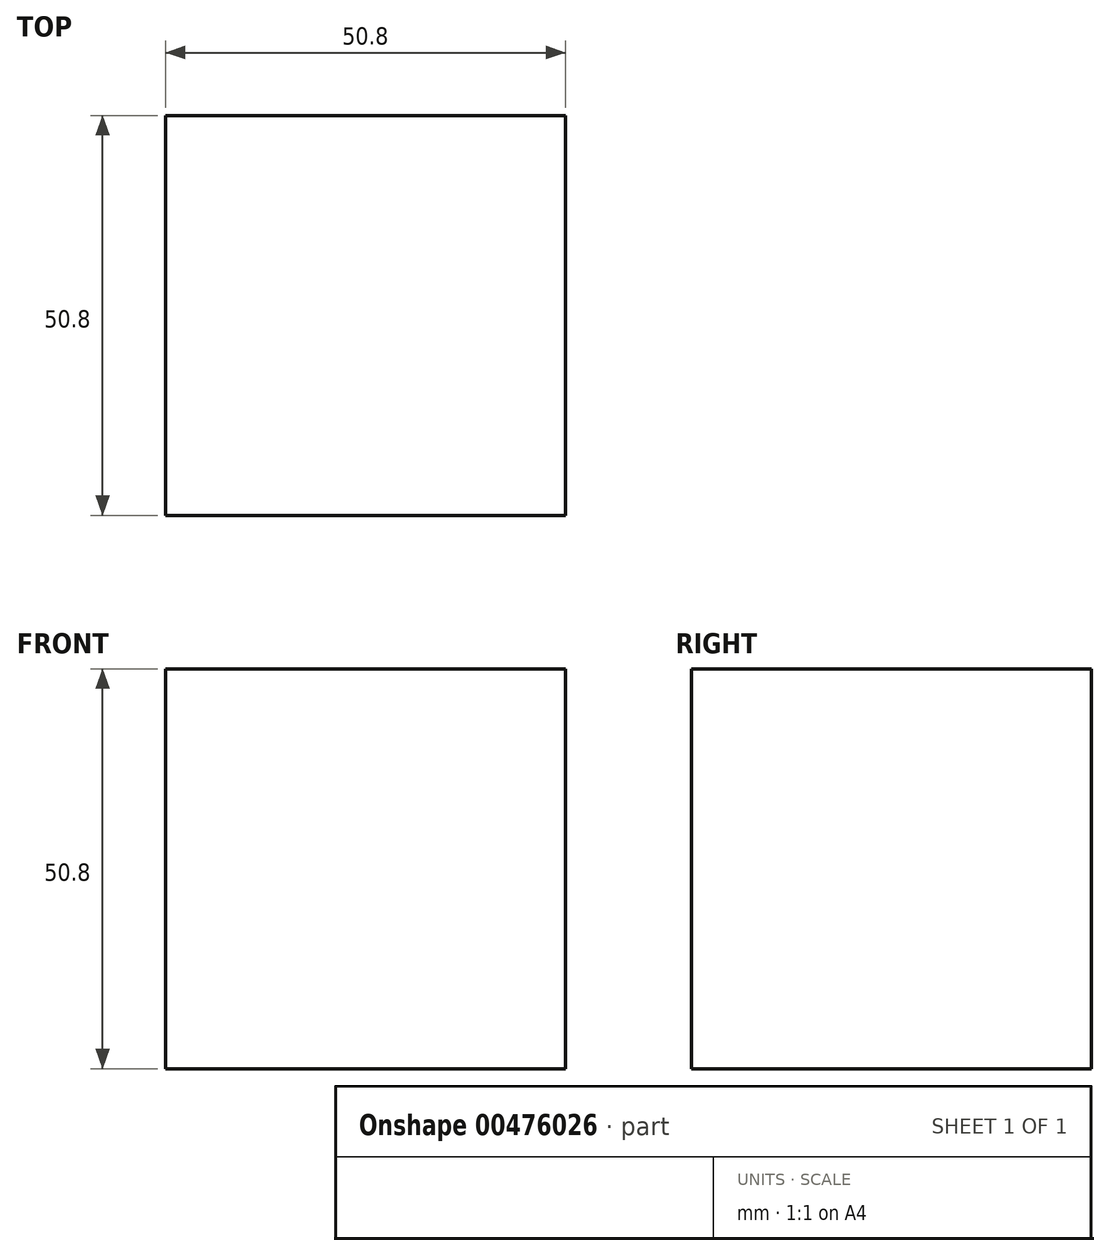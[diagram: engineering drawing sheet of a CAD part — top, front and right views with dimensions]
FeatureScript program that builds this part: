
annotation { "Feature Type Name" : "Feature", "Feature Type Description" : "" }
export const myFeature = defineFeature(function(context is Context, id is Id, definition is map)
    precondition{}
    {
        {
            var Q0;
            Q0=qCreatedBy(makeId("Front.planeOp"),FACE);
            var sketch = newSketch(context, id + "F0", { "sketchPlane" : qUnion([Q0])});
            skLineSegment(sketch, "E0.bottom", {"start": v(-32.94, 38.94) * mm, "end": v(17.86, 38.94) * mm});
            skLineSegment(sketch, "E0.top", {"start": v(-32.94, -11.86) * mm, "end": v(17.86, -11.86) * mm});
            skLineSegment(sketch, "E0.left", {"start": v(-32.94, 38.94) * mm, "end": v(-32.94, -11.86) * mm});
            skLineSegment(sketch, "E0.right", {"start": v(17.86, 38.94) * mm, "end": v(17.86, -11.86) * mm});
            skSolve(sketch);
        }
        {
            var Q0;
            Q0 = qSketchRegion(id + "F0", true);
            extrude(context, id + "F1", {"entities" : qUnion([Q0]), "depth" : 50.8 * mm});
        }
    });
